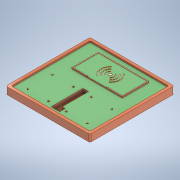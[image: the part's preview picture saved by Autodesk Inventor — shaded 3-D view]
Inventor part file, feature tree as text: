
AUTODESK INVENTOR PART (.ipt)
format: ipt  version: 2021 (Build 250183000, 183)  size: 330,240 bytes
history: native  units: mm
features: extrude x9, sketch x8, fillet x2, chamfer x2
ambient origin geometry x8: Origin, YZ Plane, XZ Plane, XY Plane, X Axis, Y Axis, Z Axis, Center Point
bodies: Solid1 (feature_tree)
feature tree (21):
  extrude  "Extrusion1"  Depth=300.0mm
  extrude  "Extrusion2"  Depth=10.0mm
  fillet  "Fillet1"  Radius=10.0mm
  fillet  "Fillet2"  Radius=10.0mm
  extrude  "Extrusion3"  Depth=5.0mm TaperAngle=0.0deg
  extrude  "Extrusion4"  Depth=5.0mm
  extrude  "Extrusion6"  Depth=20.0mm
  extrude  "Extrusion9"  Depth=50.0mm
  extrude  "Extrusion11"  Depth=2.5mm
  extrude  "Extrusion12"  Depth=2.5mm
  extrude  "Extrusion13"  Depth=2.5mm
  chamfer  "Chamfer1"  Distance=1.0mm
  chamfer  "Chamfer2"  Distance=70.0mm
  sketch  "Sketch1"  dims[d0=300.0mm d1=300.0mm]
  sketch  "Sketch2"  dims[d2=25.0mm d3=0.0mm d4=10.0mm d5=10.0mm d6=10.0mm]
  sketch  "Sketch3"  dims[d7=10.0mm d8=5.0mm d9=0.0mm]
  sketch  "Sketch5"  dims[d10=5.0mm d11=5.0mm]
  sketch  "Sketch8"  dims[d12=95.0mm d13=20.0mm]
  sketch  "Sketch11"  dims[d14=50.0mm d15=50.0mm]
  sketch  "Sketch12"  dims[d16=5.0mm d17=0.0mm d18=2.5mm]
  sketch  "Sketch13"  dims[d19=2.5mm d20=2.5mm d21=2.5mm d22=1.0mm d23=0.0mm d47=70.0mm d48=65.0mm d49=50.0mm d50=45.0mm d51=30.0mm d52=25.0mm d53=10.0mm d55=0.5mm d56=0.0mm d64=69.0mm d72=34.25mm d74=34.25mm d75=1.0mm d76=0.0mm d85=6.0mm d86=0.0mm d87=50.0mm d90=94.0mm d91=5.0mm d92=5.0mm d93=5.0mm d97=15.0mm d98=0.0mm d100=10.0mm d101=10.0mm d105=70.0mm d106=5.0mm d107=5.0mm d108=5.0mm d109=5.0mm d110=70.0mm d111=5.0mm d112=70.0mm d113=5.0mm d114=15.0mm d115=0.0mm d116=4.0mm d117=2.0mm d118=45.0deg d119=4.0mm d120=2.0mm d121=45.0deg]
